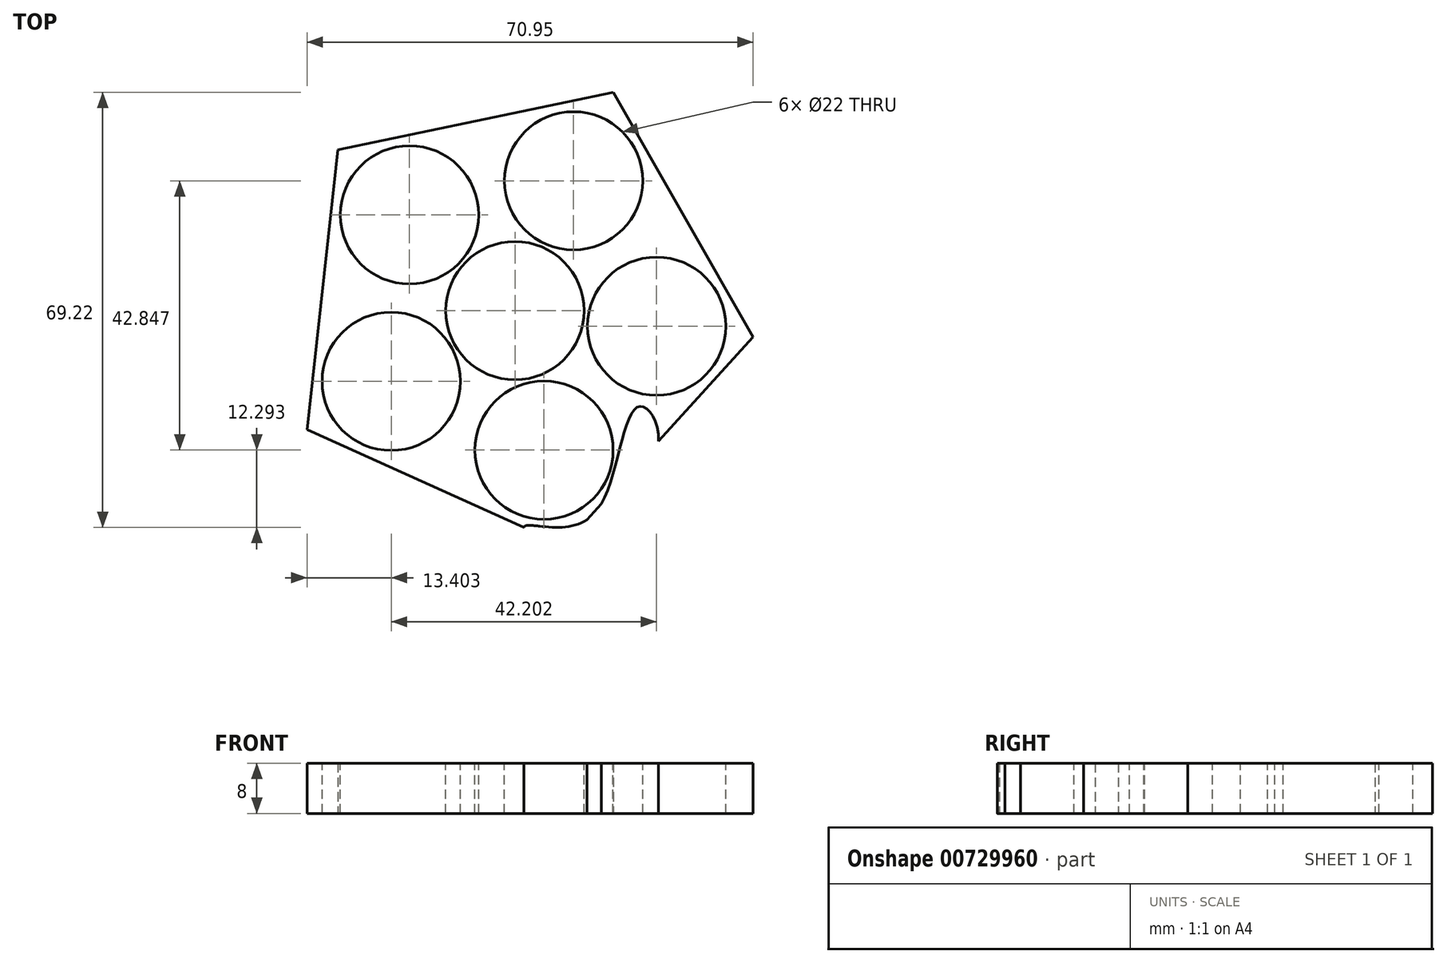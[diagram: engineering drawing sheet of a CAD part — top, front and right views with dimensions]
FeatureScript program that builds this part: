
annotation { "Feature Type Name" : "Feature", "Feature Type Description" : "" }
export const myFeature = defineFeature(function(context is Context, id is Id, definition is map)
    precondition{}
    {
        {
            var Q0;
            Q0=qCreatedBy(makeId("Top.planeOp"),FACE);
            var sketch = newSketch(context, id + "F0", { "sketchPlane" : qUnion([Q0])});
            skCircle(sketch, "E0.cCircle", {"center": v(0, 0) * mm, "radius": 38.1 * mm, "construction": true});
            skLineSegment(sketch, "E0.0", {"start": v(-33.08, -18.9) * mm, "end": v(-28.2, 25.62) * mm});
            skLineSegment(sketch, "E0.1", {"start": v(-28.2, 25.62) * mm, "end": v(15.66, 34.74) * mm});
            skLineSegment(sketch, "E0.2", {"start": v(15.66, 34.74) * mm, "end": v(37.87, -4.16) * mm});
            skLineSegment(sketch, "E0.3", {"start": v(37.87, -4.16) * mm, "end": v(7.75, -37.3) * mm});
            skLineSegment(sketch, "E0.4", {"start": v(7.75, -37.3) * mm, "end": v(-33.08, -18.9) * mm});
            skSolve(sketch);
        }
        {
            var Q0;
            Q0 = qSketchRegion(id + "F0", true);
            extrude(context, id + "F1", {"entities" : qUnion([Q0]), "depth" : 8 * mm, "offsetDistance" : 25.4 * mm});
        }
        {
            var Q0;
            Q0=makeQuery(id+"F1.opExtrude","CAP_FACE",FACE,{"disambiguationData":[OSD([sQuery(id+"F0.wireOp",EDGE,"E0.0"),sQuery(id+"F0.wireOp",EDGE,"E0.1"),sQuery(id+"F0.wireOp",EDGE,"E0.2"),sQuery(id+"F0.wireOp",EDGE,"E0.3"),sQuery(id+"F0.wireOp",EDGE,"E0.4")])],"isStart":false});
            var sketch = newSketch(context, id + "F2", { "sketchPlane" : qUnion([Q0])});
            skCircle(sketch, "E1", {"center": v(9.31, 20.66) * mm, "radius": 11 * mm});
            skCircle(sketch, "E2.1.0", {"center": v(-16.77, 15.24) * mm, "radius": 11 * mm});
            skCircle(sketch, "E2.2.0", {"center": v(-19.68, -11.24) * mm, "radius": 11 * mm});
            skCircle(sketch, "E2.3.0", {"center": v(4.61, -22.19) * mm, "radius": 11 * mm});
            skCircle(sketch, "E2.4.0", {"center": v(22.53, -2.47) * mm, "radius": 11 * mm});
            skPoint(sketch, "E2.center", {"position": v(0, 0) * mm});
            skCircle(sketch, "E3", {"center": v(0, 0) * mm, "radius": 11 * mm});
            skLineSegment(sketch, "E4", {"start": v(15.66, 34.74) * mm, "end": v(-12.67, -28.1) * mm});
            skSolve(sketch);
        }
        {
            var Q0;
            Q0 = qSketchRegion(id + "F0", true);
            extrude(context, id + "F3", {"entities" : qUnion([Q0]), "operationType" : NewBodyOperationType.ADD, "depth" : 7.62 * mm, "offsetDistance" : 25.4 * mm});
        }
        {
            var Q0;
            Q0 = qSketchRegion(id + "F2", true);
            extrude(context, id + "F4", {"entities" : qUnion([Q0]), "operationType" : NewBodyOperationType.REMOVE, "endBound" : BoundingType.THROUGH_ALL, "oppositeDirection" : true, "depth" : 25.4 * mm, "offsetDistance" : 25.4 * mm});
        }
        {
            var Q0;
            Q0=makeQuery(id+"F1.opExtrude","CAP_FACE",FACE,{"disambiguationData":[OSD([sQuery(id+"F0.wireOp",EDGE,"E0.0"),sQuery(id+"F0.wireOp",EDGE,"E0.1"),sQuery(id+"F0.wireOp",EDGE,"E0.2"),sQuery(id+"F0.wireOp",EDGE,"E0.3"),sQuery(id+"F0.wireOp",EDGE,"E0.4")])],"isStart":false});
            var sketch = newSketch(context, id + "F5", { "sketchPlane" : qUnion([Q0])});
            skFitSpline(sketch, "E5", {"points": [v(22.81, -20.73) * mm, v(19.49, -15.34) * mm, v(13.7, -30.75) * mm, v(5.94, -34.45) * mm, v(1.43, -34.45) * mm, v(7.75, -37.3) * mm, v(22.81, -20.73) * mm]});
            skSolve(sketch);
        }
        {
            var Q0;
            Q0 = qSketchRegion(id + "F5", true);
            extrude(context, id + "F6", {"entities" : qUnion([Q0]), "operationType" : NewBodyOperationType.REMOVE, "endBound" : BoundingType.THROUGH_ALL, "oppositeDirection" : true, "depth" : 25.4 * mm, "offsetDistance" : 25.4 * mm});
        }
    });
